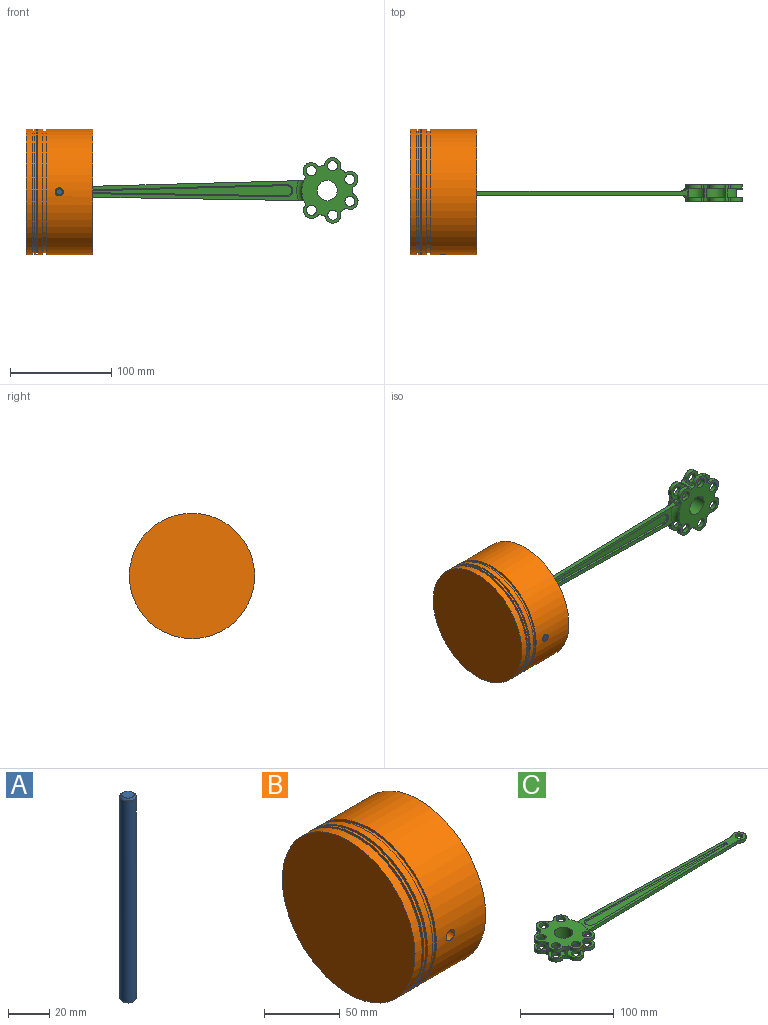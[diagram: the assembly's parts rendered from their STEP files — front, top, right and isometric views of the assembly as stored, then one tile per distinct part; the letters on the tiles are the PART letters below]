
ASSEMBLY  parts=3 mates=3
PART A: 5 faces, bbox 8x8x122 mm
  f0: plane 6x6mm, normal (0,0,-1), area 28.3mm2, adj f1
  f1: cone r=4mm half-angle=45deg, axis (0,0,1), area 31.1mm2, adj f0,f3
  f2: cone r=4mm half-angle=45deg, axis (0,0,-1), area 31.1mm2, adj f3,f4
  f3: cylinder r=4mm len=120mm, axis (0,0,-1), area 3015.9mm2, adj f1,f2
  f4: plane 6x6mm, normal (0,0,1), area 28.3mm2, adj f2
PART B: 19 faces, bbox 66x124x124 mm
  f0: cylinder r=56mm len=112mm, axis (-1,0,0), area 21010.4mm2, adj f11,f12,f13,f14
  f1: plane 124x124mm, normal (-1,0,0), area 12076.3mm2, adj f2
  f2: cylinder r=62mm len=124mm, axis (-1,0,0), area 2597.1mm2, adj f1,f3
  f3: plane 124x124mm, normal (1,0,0), area 640.5mm2, adj f2,f15
  f4: plane 124x124mm, normal (-1,0,0), area 640.5mm2, adj f15,f16
  f5: plane 124x124mm, normal (1,0,0), area 640.5mm2, adj f16,f17
  f6: plane 124x124mm, normal (-1,0,0), area 640.5mm2, adj f17,f18
  f7: plane 124x124mm, normal (1,0,0), area 640.5mm2, adj f10,f18
  f8: plane 124x124mm, normal (-1,0,0), area 640.5mm2, adj f9,f10
  f9: cylinder r=62mm len=124mm, axis (-1,0,0), area 17818.1mm2, adj f8,f11,f13,f14
  f10: cylinder r=60.33mm len=120.67mm, axis (-1,0,0), area 1263.6mm2, adj f7,f8
  f11: cylinder r=4mm len=8mm, axis (0,1,0), area 150.8mm2, adj f0,f9
  f12: plane 112x112mm, normal (1,0,0), area 9852mm2, adj f0
  f13: plane 124x124mm, normal (1,0,0), area 2224.2mm2, adj f0,f9
  f14: cylinder r=4mm len=8mm, axis (0,1,0), area 150.8mm2, adj f0,f9
  f15: cylinder r=60.33mm len=120.67mm, axis (-1,0,0), area 631.8mm2, adj f3,f4
  f16: cylinder r=62mm len=124mm, axis (-1,0,0), area 649.3mm2, adj f4,f5
  f17: cylinder r=60.33mm len=120.67mm, axis (-1,0,0), area 631.8mm2, adj f5,f6
  f18: cylinder r=62mm len=124mm, axis (-1,0,0), area 1947.8mm2, adj f6,f7
PART C: 103 faces, bbox 303.7x65.4x21.8 mm
  f0: plane 233.34x14.67mm, normal (0.02,1,0), area 942.6mm2, adj f17,f28,f70,f74,f96,f100
  f1: plane 233.34x14.67mm, normal (0.02,-1,0), area 942.6mm2, adj f17,f28,f73,f74,f96,f100
  f2: cylinder r=10mm len=16.41mm, axis (0,0,-1), area 219.1mm2, adj f27,f28,f65,f101
  f3: cylinder r=10mm len=16.41mm, axis (0,0,-1), area 219.1mm2, adj f22,f23,f28,f46
  f4: cylinder r=5mm len=10mm, axis (0,0,-1), area 125.7mm2, adj f8,f24
  f5: cylinder r=5mm len=10mm, axis (0,0,-1), area 125.7mm2, adj f8,f27
  f6: cylinder r=5mm len=10mm, axis (0,0,-1), area 125.7mm2, adj f8,f22
  f7: cylinder r=5mm len=10mm, axis (0,0,-1), area 125.7mm2, adj f10,f21
  f8: plane 64.75x55.52mm, normal (0,0,-1), area 1827mm2, adj f4,f5,f6,f9,f13,f14,f28,f29
  f9: cylinder r=10mm len=20mm, axis (0,0,1), area 1005.3mm2, adj f8,f10
  f10: plane 64.75x55.52mm, normal (0,0,1), area 1827mm2, adj f7,f9,f11,f12,f28,f32,f33,f35
  f11: cylinder r=5mm len=10mm, axis (0,0,-1), area 125.7mm2, adj f10,f26
  f12: cylinder r=5mm len=10mm, axis (0,0,-1), area 125.7mm2, adj f10,f97
  f13: cylinder r=5mm len=10mm, axis (0,0,-1), area 125.7mm2, adj f8,f19
  f14: cylinder r=5mm len=10mm, axis (0,0,-1), area 125.7mm2, adj f8,f15
  f15: plane 19.11x18mm, normal (0,0,1), area 173.3mm2, adj f14,f16,f39,f46,f47,f49,f51
  f16: cylinder r=10mm len=19.11mm, axis (0,0,-1), area 219.1mm2, adj f15,f21,f46,f51
  f17: plane 244.15x19.64mm, normal (0,0,-1), area 1845.8mm2, adj f0,f1,f70,f71,f73,f91,f92,f93
  f18: plane 19.11x18mm, normal (0,0,1), area 173.3mm2, adj f34,f59,f60,f63,f65,f87,f98
  f19: plane 18x18mm, normal (0,0,1), area 173.3mm2, adj f13,f20,f38,f50,f51,f55,f69
  f20: cylinder r=10mm len=17.96mm, axis (0,0,-1), area 219.1mm2, adj f19,f26,f51,f55
  f21: plane 19.11x18mm, normal (0,0,-1), area 173.3mm2, adj f7,f16,f40,f45,f46,f48,f51
  f22: plane 18x18mm, normal (0,0,1), area 173.3mm2, adj f3,f6,f28,f41,f44,f46,f68
  f23: plane 18x18mm, normal (0,0,-1), area 173.3mm2, adj f3,f28,f42,f43,f46,f67,f102
  f24: plane 18x18mm, normal (0,0,1), area 173.3mm2, adj f4,f25,f36,f54,f55,f57,f60
  f25: cylinder r=10mm len=17.96mm, axis (0,0,-1), area 219.1mm2, adj f24,f55,f60,f97
  f26: plane 18x18mm, normal (0,0,-1), area 173.3mm2, adj f11,f20,f37,f51,f52,f53,f55
  f27: plane 18x18mm, normal (0,0,1), area 173.3mm2, adj f2,f5,f28,f29,f30,f31,f65
  f28: cylinder r=25mm len=24.77mm, axis (0,0,1), area 119.1mm2, adj f0,f1,f2,f3,f8,f10,f22,f23
  f29: cylinder r=8mm len=14.21mm, axis (0,0,-1), area 100mm2, adj f8,f27,f30,f31
  f30: cylinder r=2mm len=4mm, axis (0,0,-1), area 9.5mm2, adj f8,f27,f28,f29
  f31: cylinder r=2mm len=4mm, axis (0,0,-1), area 9.5mm2, adj f8,f27,f29,f65
  f32: cylinder r=8mm len=14.21mm, axis (0,0,-1), area 100mm2, adj f10,f64,f66,f101
  f33: cylinder r=8mm len=15.79mm, axis (0,0,-1), area 100mm2, adj f10,f61,f62,f99
  f34: cylinder r=8mm len=15.79mm, axis (0,0,-1), area 100mm2, adj f8,f18,f59,f63
  f35: cylinder r=8mm len=15.18mm, axis (0,0,-1), area 100mm2, adj f10,f56,f58,f97
  f36: cylinder r=8mm len=15.18mm, axis (0,0,-1), area 100mm2, adj f8,f24,f54,f57
  f37: cylinder r=8mm len=15.18mm, axis (0,0,-1), area 100mm2, adj f10,f26,f52,f53
  f38: cylinder r=8mm len=15.18mm, axis (0,0,-1), area 100mm2, adj f8,f19,f50,f69
  f39: cylinder r=8mm len=15.79mm, axis (0,0,-1), area 100mm2, adj f8,f15,f47,f49
  f40: cylinder r=8mm len=15.79mm, axis (0,0,-1), area 100mm2, adj f10,f21,f45,f48
  f41: cylinder r=8mm len=14.21mm, axis (0,0,-1), area 100mm2, adj f8,f22,f44,f68
  f42: cylinder r=8mm len=14.21mm, axis (0,0,-1), area 100mm2, adj f10,f23,f43,f67
  f43: cylinder r=2mm len=4mm, axis (0,0,-1), area 9.5mm2, adj f10,f23,f42,f46
  f44: cylinder r=2mm len=4mm, axis (0,0,-1), area 9.5mm2, adj f8,f22,f41,f46
  f45: cylinder r=2mm len=4mm, axis (0,0,-1), area 9.5mm2, adj f10,f21,f40,f46
  f46: cylinder r=25mm len=16mm, axis (0,0,1), area 46.2mm2, adj f3,f8,f10,f15,f16,f21,f22,f23
  f47: cylinder r=2mm len=4mm, axis (0,0,-1), area 9.5mm2, adj f8,f15,f39,f46
  f48: cylinder r=2mm len=4mm, axis (0,0,-1), area 9.5mm2, adj f10,f21,f40,f51
  f49: cylinder r=2mm len=4mm, axis (0,0,-1), area 9.5mm2, adj f8,f15,f39,f51
  f50: cylinder r=2mm len=4mm, axis (0,0,-1), area 9.5mm2, adj f8,f19,f38,f51
  f51: cylinder r=25mm len=16mm, axis (0,0,1), area 46.2mm2, adj f8,f10,f15,f16,f19,f20,f21,f26
  f52: cylinder r=2mm len=4mm, axis (0,0,-1), area 9.5mm2, adj f10,f26,f37,f51
  f53: cylinder r=2mm len=4mm, axis (0,0,-1), area 9.5mm2, adj f10,f26,f37,f55
  f54: cylinder r=2mm len=4mm, axis (0,0,-1), area 9.5mm2, adj f8,f24,f36,f55
  f55: cylinder r=25mm len=16mm, axis (0,0,1), area 46.2mm2, adj f8,f10,f19,f20,f24,f25,f26,f53
  f56: cylinder r=2mm len=4mm, axis (0,0,-1), area 9.5mm2, adj f10,f35,f55,f97
  f57: cylinder r=2mm len=4mm, axis (0,0,-1), area 9.5mm2, adj f8,f24,f36,f60
  f58: cylinder r=2mm len=4mm, axis (0,0,-1), area 9.5mm2, adj f10,f35,f60,f97
  f59: cylinder r=2mm len=4mm, axis (0,0,-1), area 9.5mm2, adj f8,f18,f34,f60
  f60: cylinder r=25mm len=16mm, axis (0,0,1), area 46.2mm2, adj f8,f10,f18,f24,f25,f57,f58,f59
  f61: cylinder r=2mm len=4mm, axis (0,0,-1), area 9.5mm2, adj f10,f33,f60,f99
  f62: cylinder r=2mm len=4mm, axis (0,0,-1), area 9.5mm2, adj f10,f33,f65,f99
  f63: cylinder r=2mm len=4mm, axis (0,0,-1), area 9.5mm2, adj f8,f18,f34,f65
  f64: cylinder r=2mm len=4mm, axis (0,0,-1), area 9.5mm2, adj f10,f32,f65,f101
  f65: cylinder r=25mm len=16mm, axis (0,0,1), area 46.2mm2, adj f2,f8,f10,f18,f27,f31,f62,f63
  f66: cylinder r=2mm len=4mm, axis (0,0,-1), area 9.5mm2, adj f10,f28,f32,f101
  f67: cylinder r=2mm len=4mm, axis (0,0,-1), area 9.5mm2, adj f10,f23,f28,f42
  f68: cylinder r=2mm len=4mm, axis (0,0,-1), area 9.5mm2, adj f8,f22,f28,f41
  f69: cylinder r=2mm len=4mm, axis (0,0,-1), area 9.5mm2, adj f8,f19,f38,f55
  f70: cylinder r=10mm len=5.45mm, axis (0,0,-1), area 22.9mm2, adj f0,f17,f95,f96
  f71: cylinder r=1.67mm len=3.33mm, axis (0,0,1), area 3.4mm2, adj f17,f80,f92,f94
  f72: cylinder r=1.67mm len=3.33mm, axis (0,0,1), area 3.4mm2, adj f76,f88,f90,f96
  f73: cylinder r=10mm len=5.45mm, axis (0,0,1), area 22.9mm2, adj f1,f17,f95,f96
  f74: torus R=30mm, axis (0,0,1), area 155.8mm2, adj f0,f1,f28,f96
  f75: torus R=5mm, axis (0,0,-1), area 28.2mm2, adj f77,f78,f84,f89
  f76: torus R=0.67mm, axis (0,0,-1), area 6.3mm2, adj f72,f77,f78,f84
  f77: cylinder r=1mm len=204.93mm, axis (-1,-0.02,0), area 321.9mm2, adj f75,f76,f84,f88
  f78: cylinder r=1mm len=204.93mm, axis (1,-0.02,0), area 321.9mm2, adj f75,f76,f84,f90
  f79: cylinder r=1mm len=204.93mm, axis (-1,0.02,0), area 321.9mm2, adj f80,f82,f83,f94
  f80: torus R=0.67mm, axis (0,0,-1), area 6.3mm2, adj f71,f79,f81,f83
  f81: cylinder r=1mm len=204.93mm, axis (-1,-0.02,0), area 321.9mm2, adj f80,f82,f83,f92
  f82: torus R=5mm, axis (0,0,-1), area 28.2mm2, adj f79,f81,f83,f93
  f83: plane 210.67x10mm, normal (0,0,-1), area 1201.9mm2, adj f79,f80,f81,f82
  f84: plane 210.67x10mm, normal (0,0,1), area 1201.9mm2, adj f75,f76,f77,f78
  f85: cylinder r=5mm len=10mm, axis (0,0,-1), area 125.7mm2, adj f10,f99
  f86: cylinder r=5mm len=10mm, axis (0,0,-1), area 125.7mm2, adj f10,f101
  f87: cylinder r=5mm len=10mm, axis (0,0,-1), area 125.7mm2, adj f8,f18
  f88: plane 204.91x4.33mm, normal (-0.02,1,0), area 136.6mm2, adj f72,f77,f89,f96
  f89: cylinder r=6mm len=12mm, axis (0,0,1), area 12.7mm2, adj f75,f88,f90,f96
  f90: plane 204.91x4.33mm, normal (-0.02,-1,0), area 136.6mm2, adj f72,f78,f89,f96
  f91: cylinder r=4mm len=8mm, axis (0,0,-1), area 100.5mm2, adj f17,f96
  f92: plane 204.91x4.33mm, normal (-0.02,1,0), area 136.6mm2, adj f17,f71,f81,f93
  f93: cylinder r=6mm len=12mm, axis (0,0,1), area 12.7mm2, adj f17,f82,f92,f94
  f94: plane 204.91x4.33mm, normal (-0.02,-1,0), area 136.6mm2, adj f17,f71,f79,f93
  f95: cylinder r=7.5mm len=15mm, axis (0,0,-1), area 127.3mm2, adj f17,f70,f73,f96
  f96: plane 244.15x19.64mm, normal (0,0,1), area 1845.8mm2, adj f0,f1,f70,f72,f73,f74,f88,f89
  f97: plane 18x18mm, normal (0,0,-1), area 173.3mm2, adj f12,f25,f35,f55,f56,f58,f60
  f98: cylinder r=10mm len=19.11mm, axis (0,0,-1), area 219.1mm2, adj f18,f60,f65,f99
  f99: plane 19.11x18mm, normal (0,0,-1), area 173.3mm2, adj f33,f60,f61,f62,f65,f85,f98
  f100: torus R=30mm, axis (0,0,1), area 155.8mm2, adj f0,f1,f17,f28
  f101: plane 18x18mm, normal (0,0,-1), area 173.3mm2, adj f2,f28,f32,f64,f65,f66,f86
  f102: cylinder r=5mm len=10mm, axis (0,0,-1), area 125.7mm2, adj f10,f23
PLACE A rot(axis=(1,0,0),90deg) t=(-277.87,147.92,-66.02)mm
PLACE B t=(-277.87,99,-16.02)mm
PLACE C rot(axis=(0,0.71,0.71),179.8deg) t=(87.4,147.92,-64.28)mm
MATE fastened A.f1 <-> B.f11  axis (0,1,0) through (-227.87,207.92,-16.02)mm
MATE planar A.f3 <-> C.f91  axis (0,1,0) through (-227.87,147.92,-16.02)mm
MATE cylindrical C.f91 <-> A.f3  axis (0,-1,0) through (-227.87,147.92,-16.02)mm
